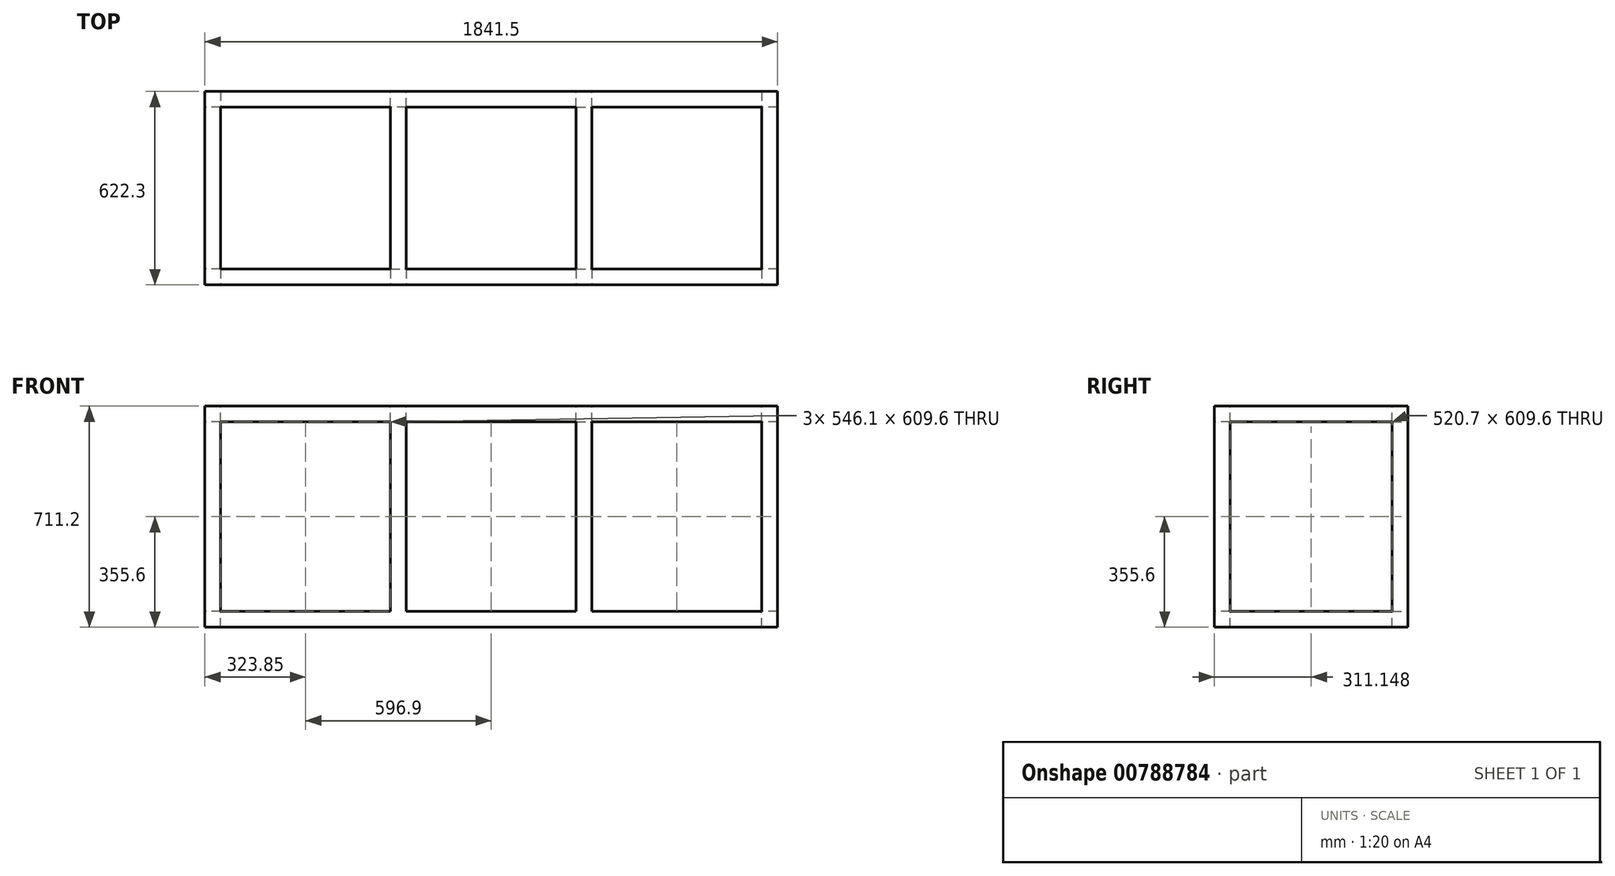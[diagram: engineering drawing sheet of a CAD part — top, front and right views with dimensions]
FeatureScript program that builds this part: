
annotation { "Feature Type Name" : "Feature", "Feature Type Description" : "" }
export const myFeature = defineFeature(function(context is Context, id is Id, definition is map)
    precondition{}
    {
        {
            var Q0;
            Q0=qCreatedBy(makeId("Top.planeOp"),FACE);
            var sketch = newSketch(context, id + "F0", { "sketchPlane" : qUnion([Q0])});
            skLineSegment(sketch, "E0.bottom", {"start": v(-106.55, -170.8) * mm, "end": v(1734.95, -170.8) * mm});
            skLineSegment(sketch, "E0.top", {"start": v(-106.55, 451.5) * mm, "end": v(1734.95, 451.5) * mm});
            skLineSegment(sketch, "E0.left", {"start": v(-106.55, -170.8) * mm, "end": v(-106.55, 451.5) * mm});
            skLineSegment(sketch, "E0.right", {"start": v(1734.95, -170.8) * mm, "end": v(1734.95, 451.5) * mm});
            skSolve(sketch);
        }
        {
            var Q0;
            Q0=makeQuery(id+"F0.imprint","IMPRINT",FACE,{"disambiguationData":[TD([[makeQuery(id+"F0.imprint","IMPRINT",EDGE,{"derivedFrom":sQuery(id+"F0.wireOp",EDGE,"E0.bottom")}),1.0]])]});
            extrude(context, id + "F1", {"entities" : qUnion([Q0]), "depth" : 711.2 * mm, "offsetDistance" : 25.4 * mm});
        }
        {
            var Q0;
            Q0=makeQuery(id+"F1.opExtrude","SWEPT_FACE",FACE,{"disambiguationData":[OSD([sQuery(id+"F0.wireOp",EDGE,"E0.bottom")])]});
            var sketch = newSketch(context, id + "F2", { "sketchPlane" : qUnion([Q0])});
            skLineSegment(sketch, "E1.bottom", {"start": v(-55.75, 660.4) * mm, "end": v(1684.15, 660.4) * mm});
            skLineSegment(sketch, "E1.top", {"start": v(-55.75, 50.8) * mm, "end": v(1684.15, 50.8) * mm});
            skLineSegment(sketch, "E1.left", {"start": v(-55.75, 660.4) * mm, "end": v(-55.75, 50.8) * mm});
            skLineSegment(sketch, "E1.right", {"start": v(1684.15, 660.4) * mm, "end": v(1684.15, 50.8) * mm});
            skSolve(sketch);
        }
        {
            var Q0;
            Q0=makeQuery(id+"F2.imprint","IMPRINT",FACE,{"disambiguationData":[TD([[makeQuery(id+"F2.imprint","IMPRINT",EDGE,{"derivedFrom":sQuery(id+"F2.wireOp",EDGE,"E1.bottom")}),-1.0]])]});
            extrude(context, id + "F3", {"entities" : qUnion([Q0]), "operationType" : NewBodyOperationType.REMOVE, "oppositeDirection" : true, "depth" : 762 * mm, "offsetDistance" : 25.4 * mm});
        }
        {
            var Q0;
            Q0=makeQuery(id+"F1.opExtrude","SWEPT_FACE",FACE,{"disambiguationData":[OSD([sQuery(id+"F0.wireOp",EDGE,"E0.left")])]});
            var sketch = newSketch(context, id + "F4", { "sketchPlane" : qUnion([Q0])});
            skLineSegment(sketch, "E2.bottom", {"start": v(-400.7, 660.4) * mm, "end": v(120, 660.4) * mm});
            skLineSegment(sketch, "E2.top", {"start": v(-400.7, 50.8) * mm, "end": v(120, 50.8) * mm});
            skLineSegment(sketch, "E2.left", {"start": v(-400.7, 660.4) * mm, "end": v(-400.7, 50.8) * mm});
            skLineSegment(sketch, "E2.right", {"start": v(120, 660.4) * mm, "end": v(120, 50.8) * mm});
            skSolve(sketch);
        }
        {
            var Q0;
            Q0=makeQuery(id+"F4.imprint","IMPRINT",FACE,{"disambiguationData":[TD([[makeQuery(id+"F4.imprint","IMPRINT",EDGE,{"derivedFrom":sQuery(id+"F4.wireOp",EDGE,"E2.bottom")}),-1.0]])]});
            extrude(context, id + "F5", {"entities" : qUnion([Q0]), "operationType" : NewBodyOperationType.REMOVE, "oppositeDirection" : true, "depth" : 2540 * mm, "offsetDistance" : 25.4 * mm});
        }
        {
            var Q0;
            Q0=makeQuery(id+"F1.opExtrude","CAP_FACE",FACE,{"disambiguationData":[OSD([sQuery(id+"F0.wireOp",EDGE,"E0.bottom"),sQuery(id+"F0.wireOp",EDGE,"E0.top"),sQuery(id+"F0.wireOp",EDGE,"E0.left"),sQuery(id+"F0.wireOp",EDGE,"E0.right")])],"isStart":false});
            var sketch = newSketch(context, id + "F6", { "sketchPlane" : qUnion([Q0])});
            skLineSegment(sketch, "E3.bottom", {"start": v(-55.75, 400.7) * mm, "end": v(1684.15, 400.7) * mm});
            skLineSegment(sketch, "E3.top", {"start": v(-55.75, -120) * mm, "end": v(1684.15, -120) * mm});
            skLineSegment(sketch, "E3.left", {"start": v(-55.75, 400.7) * mm, "end": v(-55.75, -120) * mm});
            skLineSegment(sketch, "E3.right", {"start": v(1684.15, 400.7) * mm, "end": v(1684.15, -120) * mm});
            skSolve(sketch);
        }
        {
            var Q0;
            Q0=makeQuery(id+"F6.imprint","IMPRINT",FACE,{"disambiguationData":[TD([[makeQuery(id+"F6.imprint","IMPRINT",EDGE,{"derivedFrom":sQuery(id+"F6.wireOp",EDGE,"E3.bottom")}),-1.0]])]});
            extrude(context, id + "F7", {"entities" : qUnion([Q0]), "operationType" : NewBodyOperationType.REMOVE, "oppositeDirection" : true, "depth" : 2540 * mm, "offsetDistance" : 25.4 * mm});
        }
        {
            var Q0;
            {var subQ1=makeQuery(id+"F3.boolean.opBoolean","COPY",FACE,{"derivedFrom":makeQuery(id+"F3.opExtrude","SWEPT_FACE",FACE,{"disambiguationData":[OSD([sQuery(id+"F2.wireOp",EDGE,"E1.bottom")])]})});Q0=makeQuery(id+"F7.boolean.opBoolean","COPY",FACE,{"disambiguationData":[TD([subQ1])],"derivedFrom":makeQuery(id+"F7.opExtrude","SWEPT_FACE",FACE,{"disambiguationData":[OSD([sQuery(id+"F6.wireOp",EDGE,"E3.bottom")])]})});}
            var sketch = newSketch(context, id + "F8", { "sketchPlane" : qUnion([Q0])});
            skLineSegment(sketch, "E4.bottom", {"start": v(490.35, 660.4) * mm, "end": v(541.15, 660.4) * mm});
            skLineSegment(sketch, "E4.top", {"start": v(490.35, 711.2) * mm, "end": v(541.15, 711.2) * mm});
            skLineSegment(sketch, "E4.left", {"start": v(490.35, 660.4) * mm, "end": v(490.35, 711.2) * mm});
            skLineSegment(sketch, "E4.right", {"start": v(541.15, 660.4) * mm, "end": v(541.15, 711.2) * mm});
            skLineSegment(sketch, "E5.bottom", {"start": v(1087.25, 660.4) * mm, "end": v(1138.05, 660.4) * mm});
            skLineSegment(sketch, "E5.top", {"start": v(1087.25, 711.2) * mm, "end": v(1138.05, 711.2) * mm});
            skLineSegment(sketch, "E5.left", {"start": v(1087.25, 660.4) * mm, "end": v(1087.25, 711.2) * mm});
            skLineSegment(sketch, "E5.right", {"start": v(1138.05, 660.4) * mm, "end": v(1138.05, 711.2) * mm});
            skSolve(sketch);
        }
        {
            var Q0;
            Q0=makeQuery(id+"F8.imprint","IMPRINT",FACE,{"disambiguationData":[TD([[makeQuery(id+"F8.imprint","IMPRINT",EDGE,{"derivedFrom":sQuery(id+"F8.wireOp",EDGE,"E4.bottom")}),-1.0]])]});
            var Q1;
            Q1=makeQuery(id+"F8.imprint","IMPRINT",FACE,{"disambiguationData":[TD([[makeQuery(id+"F8.imprint","IMPRINT",EDGE,{"derivedFrom":sQuery(id+"F8.wireOp",EDGE,"E5.bottom")}),-1.0]])]});
            extrude(context, id + "F9", {"entities" : qUnion([Q0, Q1]), "operationType" : NewBodyOperationType.ADD, "depth" : 520.7 * mm, "offsetDistance" : 25.4 * mm});
        }
        {
            var Q0;
            {var subQ3=makeQuery(id+"F3.boolean.opBoolean","COPY",FACE,{"derivedFrom":makeQuery(id+"F3.opExtrude","SWEPT_FACE",FACE,{"disambiguationData":[OSD([sQuery(id+"F2.wireOp",EDGE,"E1.bottom")])]})});var subQ4=makeQuery(id+"F5.opExtrude","SWEPT_FACE",FACE,{"disambiguationData":[OSD([sQuery(id+"F4.wireOp",EDGE,"E2.bottom")])]});var subQ11=makeQuery(id+"F5.boolean.opBoolean","MERGE",FACE,{"derivedFrom":[subQ3,subQ4]});Q0=makeQuery(id+"F9.boolean.opBoolean","MERGE",FACE,{"derivedFrom":[makeQuery(id+"F7.boolean.opBoolean","SPLIT",FACE,{"disambiguationData":[TD([makeQuery(id+"F1.opExtrude","SWEPT_FACE",FACE,{"disambiguationData":[OSD([sQuery(id+"F0.wireOp",EDGE,"E0.bottom")])]})])],"derivedFrom":subQ11}),makeQuery(id+"F7.boolean.opBoolean","SPLIT",FACE,{"disambiguationData":[TD([makeQuery(id+"F1.opExtrude","SWEPT_FACE",FACE,{"disambiguationData":[OSD([sQuery(id+"F0.wireOp",EDGE,"E0.top")])]})])],"derivedFrom":subQ11}),makeQuery(id+"F9.opExtrude","SWEPT_FACE",FACE,{"disambiguationData":[OSD([sQuery(id+"F8.wireOp",EDGE,"E4.bottom")])]}),makeQuery(id+"F9.opExtrude","SWEPT_FACE",FACE,{"disambiguationData":[OSD([sQuery(id+"F8.wireOp",EDGE,"E5.bottom")])]})]});}
            var sketch = newSketch(context, id + "F10", { "sketchPlane" : qUnion([Q0])});
            skLineSegment(sketch, "E6.bottom", {"start": v(1087.25, -400.7) * mm, "end": v(1138.05, -400.7) * mm});
            skLineSegment(sketch, "E6.top", {"start": v(1087.25, -451.5) * mm, "end": v(1138.05, -451.5) * mm});
            skLineSegment(sketch, "E6.left", {"start": v(1087.25, -400.7) * mm, "end": v(1087.25, -451.5) * mm});
            skLineSegment(sketch, "E6.right", {"start": v(1138.05, -400.7) * mm, "end": v(1138.05, -451.5) * mm});
            skLineSegment(sketch, "E7.bottom", {"start": v(541.15, -400.7) * mm, "end": v(490.35, -400.7) * mm});
            skLineSegment(sketch, "E7.top", {"start": v(541.15, -451.5) * mm, "end": v(490.35, -451.5) * mm});
            skLineSegment(sketch, "E7.left", {"start": v(541.15, -400.7) * mm, "end": v(541.15, -451.5) * mm});
            skLineSegment(sketch, "E7.right", {"start": v(490.35, -400.7) * mm, "end": v(490.35, -451.5) * mm});
            skSolve(sketch);
        }
        {
            var Q0;
            Q0=makeQuery(id+"F10.imprint","IMPRINT",FACE,{"disambiguationData":[TD([[makeQuery(id+"F10.imprint","IMPRINT",EDGE,{"derivedFrom":sQuery(id+"F10.wireOp",EDGE,"E6.bottom")}),-1.0]])]});
            var Q1;
            Q1=makeQuery(id+"F10.imprint","IMPRINT",FACE,{"disambiguationData":[TD([[makeQuery(id+"F10.imprint","IMPRINT",EDGE,{"derivedFrom":sQuery(id+"F10.wireOp",EDGE,"E7.bottom")}),1.0]])]});
            extrude(context, id + "F11", {"entities" : qUnion([Q0, Q1]), "operationType" : NewBodyOperationType.ADD, "depth" : 609.6 * mm, "offsetDistance" : 25.4 * mm});
        }
        {
            var Q0;
            {var subQ0=makeQuery(id+"F5.opExtrude","SWEPT_FACE",FACE,{"disambiguationData":[OSD([sQuery(id+"F4.wireOp",EDGE,"E2.bottom")])]});var subQ1=makeQuery(id+"F3.boolean.opBoolean","COPY",FACE,{"derivedFrom":makeQuery(id+"F3.opExtrude","SWEPT_FACE",FACE,{"disambiguationData":[OSD([sQuery(id+"F2.wireOp",EDGE,"E1.bottom")])]})});var subQ2=makeQuery(id+"F3.boolean.opBoolean","COPY",FACE,{"derivedFrom":makeQuery(id+"F3.opExtrude","SWEPT_FACE",FACE,{"disambiguationData":[OSD([sQuery(id+"F2.wireOp",EDGE,"E1.right")])]})});var subQ3=sQuery(id+"F0.wireOp",EDGE,"E0.right");var subQ4=sQuery(id+"F0.wireOp",EDGE,"E0.left");var subQ5=sQuery(id+"F0.wireOp",EDGE,"E0.top");var subQ6=sQuery(id+"F0.wireOp",EDGE,"E0.bottom");var subQ8=makeQuery(id+"F1.opExtrude","SWEPT_FACE",FACE,{"disambiguationData":[OSD([subQ3])]});var subQ9=makeQuery(id+"F3.boolean.opBoolean","COPY",FACE,{"derivedFrom":makeQuery(id+"F3.opExtrude","SWEPT_FACE",FACE,{"disambiguationData":[OSD([sQuery(id+"F2.wireOp",EDGE,"E1.top")])]})});var subQ13=makeQuery(id+"F5.opExtrude","SWEPT_FACE",FACE,{"disambiguationData":[OSD([sQuery(id+"F4.wireOp",EDGE,"E2.right")])]});var subQ14=makeQuery(id+"F5.boolean.opBoolean","COPY",FACE,{"disambiguationData":[TD([subQ8])],"derivedFrom":subQ13});var subQ15=makeQuery(id+"F7.opExtrude","SWEPT_FACE",FACE,{"disambiguationData":[OSD([sQuery(id+"F6.wireOp",EDGE,"E3.bottom")])]});var subQ16=makeQuery(id+"F7.opExtrude","SWEPT_FACE",FACE,{"disambiguationData":[OSD([sQuery(id+"F6.wireOp",EDGE,"E3.top")])]});var subQ17=makeQuery(id+"F7.opExtrude","SWEPT_FACE",FACE,{"disambiguationData":[OSD([sQuery(id+"F6.wireOp",EDGE,"E3.right")])]});var subQ18=makeQuery(id+"F9.opExtrude","SWEPT_FACE",FACE,{"disambiguationData":[OSD([sQuery(id+"F8.wireOp",EDGE,"E5.bottom")])]});var subQ19=makeQuery(id+"F3.boolean.opBoolean","COPY",FACE,{"derivedFrom":makeQuery(id+"F3.opExtrude","SWEPT_FACE",FACE,{"disambiguationData":[OSD([sQuery(id+"F2.wireOp",EDGE,"E1.left")])]})});var subQ20=makeQuery(id+"F7.opExtrude","SWEPT_FACE",FACE,{"disambiguationData":[OSD([sQuery(id+"F6.wireOp",EDGE,"E3.left")])]});var subQ21=makeQuery(id+"F1.opExtrude","SWEPT_FACE",FACE,{"disambiguationData":[OSD([subQ4])]});var subQ22=makeQuery(id+"F5.boolean.opBoolean","COPY",FACE,{"disambiguationData":[TD([subQ21])],"derivedFrom":subQ13});var subQ24=makeQuery(id+"F9.opExtrude","SWEPT_FACE",FACE,{"disambiguationData":[OSD([sQuery(id+"F8.wireOp",EDGE,"E4.bottom")])]});var subQ25=makeQuery(id+"F1.opExtrude","SWEPT_FACE",FACE,{"disambiguationData":[OSD([subQ6])]});var subQ26=makeQuery(id+"F5.boolean.opBoolean","MERGE",FACE,{"derivedFrom":[subQ1,subQ0]});Q0=makeQuery(id+"F11.boolean.opBoolean","SPLIT",FACE,{"disambiguationData":[TD([subQ25,subQ1,subQ19,subQ2,subQ0,subQ22,subQ14,makeQuery(id+"F7.boolean.opBoolean","COPY",FACE,{"disambiguationData":[TD([subQ1])],"derivedFrom":subQ15}),makeQuery(id+"F7.boolean.opBoolean","COPY",FACE,{"disambiguationData":[TD([subQ9])],"derivedFrom":subQ15}),makeQuery(id+"F7.boolean.opBoolean","COPY",FACE,{"disambiguationData":[TD([subQ1])],"derivedFrom":subQ16}),makeQuery(id+"F7.boolean.opBoolean","COPY",FACE,{"disambiguationData":[TD([subQ1])],"derivedFrom":subQ20}),makeQuery(id+"F7.boolean.opBoolean","COPY",FACE,{"disambiguationData":[TD([subQ1])],"derivedFrom":subQ17}),subQ24,makeQuery(id+"F9.opExtrude","SWEPT_FACE",FACE,{"disambiguationData":[OSD([sQuery(id+"F8.wireOp",EDGE,"E4.left")])]}),makeQuery(id+"F9.opExtrude","SWEPT_FACE",FACE,{"disambiguationData":[OSD([sQuery(id+"F8.wireOp",EDGE,"E4.right")])]}),subQ18,makeQuery(id+"F9.opExtrude","SWEPT_FACE",FACE,{"disambiguationData":[OSD([sQuery(id+"F8.wireOp",EDGE,"E5.left")])]}),makeQuery(id+"F9.opExtrude","SWEPT_FACE",FACE,{"disambiguationData":[OSD([sQuery(id+"F8.wireOp",EDGE,"E5.right")])]}),makeQuery(id+"F11.opExtrude","SWEPT_FACE",FACE,{"disambiguationData":[OSD([sQuery(id+"F10.wireOp",EDGE,"E6.bottom")])]}),makeQuery(id+"F11.opExtrude","SWEPT_FACE",FACE,{"disambiguationData":[OSD([sQuery(id+"F10.wireOp",EDGE,"E6.left")])]}),makeQuery(id+"F11.opExtrude","SWEPT_FACE",FACE,{"disambiguationData":[OSD([sQuery(id+"F10.wireOp",EDGE,"E6.right")])]}),makeQuery(id+"F11.opExtrude","SWEPT_FACE",FACE,{"disambiguationData":[OSD([sQuery(id+"F10.wireOp",EDGE,"E7.bottom")])]}),makeQuery(id+"F11.opExtrude","SWEPT_FACE",FACE,{"disambiguationData":[OSD([sQuery(id+"F10.wireOp",EDGE,"E7.left")])]}),makeQuery(id+"F11.opExtrude","SWEPT_FACE",FACE,{"disambiguationData":[OSD([sQuery(id+"F10.wireOp",EDGE,"E7.right")])]})])],"derivedFrom":makeQuery(id+"F9.boolean.opBoolean","MERGE",FACE,{"derivedFrom":[makeQuery(id+"F7.boolean.opBoolean","SPLIT",FACE,{"disambiguationData":[TD([subQ25])],"derivedFrom":subQ26}),makeQuery(id+"F7.boolean.opBoolean","SPLIT",FACE,{"disambiguationData":[TD([makeQuery(id+"F1.opExtrude","SWEPT_FACE",FACE,{"disambiguationData":[OSD([subQ5])]})])],"derivedFrom":subQ26}),subQ24,subQ18]})});}
            var sketch = newSketch(context, id + "F12", { "sketchPlane" : qUnion([Q0])});
            skLineSegment(sketch, "E8.bottom", {"start": v(490.35, 120) * mm, "end": v(541.15, 120) * mm});
            skLineSegment(sketch, "E8.top", {"start": v(490.35, 170.8) * mm, "end": v(541.15, 170.8) * mm});
            skLineSegment(sketch, "E8.left", {"start": v(490.35, 120) * mm, "end": v(490.35, 170.8) * mm});
            skLineSegment(sketch, "E8.right", {"start": v(541.15, 120) * mm, "end": v(541.15, 170.8) * mm});
            skLineSegment(sketch, "E9.bottom", {"start": v(1087.25, 120) * mm, "end": v(1138.05, 120) * mm});
            skLineSegment(sketch, "E9.top", {"start": v(1087.25, 170.8) * mm, "end": v(1138.05, 170.8) * mm});
            skLineSegment(sketch, "E9.left", {"start": v(1087.25, 120) * mm, "end": v(1087.25, 170.8) * mm});
            skLineSegment(sketch, "E9.right", {"start": v(1138.05, 120) * mm, "end": v(1138.05, 170.8) * mm});
            skSolve(sketch);
        }
        {
            var Q0;
            Q0=makeQuery(id+"F12.imprint","IMPRINT",FACE,{"disambiguationData":[TD([[makeQuery(id+"F12.imprint","IMPRINT",EDGE,{"derivedFrom":sQuery(id+"F12.wireOp",EDGE,"E8.bottom")}),1.0]])]});
            var Q1;
            Q1=makeQuery(id+"F12.imprint","IMPRINT",FACE,{"disambiguationData":[TD([[makeQuery(id+"F12.imprint","IMPRINT",EDGE,{"derivedFrom":sQuery(id+"F12.wireOp",EDGE,"E9.bottom")}),1.0]])]});
            extrude(context, id + "F13", {"entities" : qUnion([Q0, Q1]), "operationType" : NewBodyOperationType.ADD, "depth" : 609.6 * mm, "offsetDistance" : 25.4 * mm});
        }
    });
